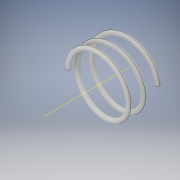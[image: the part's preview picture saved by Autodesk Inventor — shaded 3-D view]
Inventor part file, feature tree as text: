
AUTODESK INVENTOR PART (.ipt)
format: ipt  version: 2019 (Build 230136000, 136)  size: 299,520 bytes
history: native  units: mm
features: other x2, helix x1, sketch x1
ambient origin geometry x8: Origin, YZ Plane, XZ Plane, XY Plane, X Axis, Y Axis, Z Axis, Center Point
bodies: Solid1 (feature_tree)
feature tree (4):
  helix  "Coil1"  [1 undecoded]
  other  "Work Axis1"
  other  "Work Axis2"
  sketch  "Sketch1"  dims[d1=3.5mm d2=4.2mm d3=10.0mm d4=3.7mm d5=20.0mm d6=0.0mm d7=90.0deg d8=90.0deg d9=0.0mm d10=0.0mm d11=3.5mm]
note: 1 required parameter value undecoded (feature->parameter linkage not recoverable at this tier; creation-order binding heuristic only, values carry confidence <= 0.55)
